annotation { "Feature Type Name" : "Feature", "Feature Type Description" : "" }
export const myFeature = defineFeature(function(context is Context, id is Id, definition is map)
    precondition{}
    {
        {
            var Q0;
            Q0=qCreatedBy(makeId("Right.planeOp"),FACE);
            var sketch = newSketch(context, id + "F0", { "sketchPlane" : qUnion([Q0])});
            skLineSegment(sketch, "E0", {"start": v(0, 0) * mm, "end": v(-381, 0) * mm});
            skLineSegment(sketch, "E1", {"start": v(0, 0) * mm, "end": v(381, 0) * mm});
            skLineSegment(sketch, "E2", {"start": v(0, 0) * mm, "end": v(0, 190.5) * mm});
            skLineSegment(sketch, "E3", {"start": v(-381, 0) * mm, "end": v(-457.2, 0) * mm});
            skLineSegment(sketch, "E4", {"start": v(-381, 0) * mm, "end": v(0, 190.5) * mm});
            skLineSegment(sketch, "E5", {"start": v(0, 190.5) * mm, "end": v(381, 0) * mm});
            skLineSegment(sketch, "E6", {"start": v(381, 0) * mm, "end": v(457.2, 0) * mm});
            skLineSegment(sketch, "E7", {"start": v(0, 190.5) * mm, "end": v(0, 228.6) * mm});
            skLineSegment(sketch, "E8", {"start": v(0, 228.6) * mm, "end": v(-457.2, 0) * mm});
            skLineSegment(sketch, "E9", {"start": v(0, 228.6) * mm, "end": v(457.2, 0) * mm});
            skLineSegment(sketch, "E10", {"start": v(-381, 0) * mm, "end": v(-381, -279.4) * mm});
            skLineSegment(sketch, "E11", {"start": v(381, 0) * mm, "end": v(381, -279.4) * mm});
            skLineSegment(sketch, "E12", {"start": v(381, -279.4) * mm, "end": v(-381, -279.4) * mm});
            skLineSegment(sketch, "E13", {"start": v(-381, -279.4) * mm, "end": v(-381, -330.2) * mm});
            skLineSegment(sketch, "E14", {"start": v(381, -279.4) * mm, "end": v(381, -330.2) * mm});
            skLineSegment(sketch, "E15", {"start": v(381, -330.2) * mm, "end": v(-381, -330.2) * mm});
            skLineSegment(sketch, "E16", {"start": v(381, -330.2) * mm, "end": v(762, -330.2) * mm});
            skLineSegment(sketch, "E17", {"start": v(762, -330.2) * mm, "end": v(762, -279.4) * mm});
            skLineSegment(sketch, "E18", {"start": v(762, -279.4) * mm, "end": v(381, -279.4) * mm});
            skLineSegment(sketch, "E19", {"start": v(762, -279.4) * mm, "end": v(762, -50.8) * mm});
            skLineSegment(sketch, "E20", {"start": v(762, -50.8) * mm, "end": v(381, 0) * mm});
            skLineSegment(sketch, "E21", {"start": v(762, -50.8) * mm, "end": v(762, -88.9) * mm});
            skLineSegment(sketch, "E22", {"start": v(762, -88.9) * mm, "end": v(381, -50.8) * mm});
            skLineSegment(sketch, "E23", {"start": v(-226.53, -279.4) * mm, "end": v(-226.53, -101.6) * mm});
            skLineSegment(sketch, "E24", {"start": v(-226.53, -101.6) * mm, "end": v(-150.33, -101.6) * mm});
            skLineSegment(sketch, "E25", {"start": v(-150.33, -101.6) * mm, "end": v(-150.33, -279.4) * mm});
            skLineSegment(sketch, "E26.0", {"start": v(-124.93, -76.2) * mm, "end": v(-124.93, -279.4) * mm});
            skLineSegment(sketch, "E26.1", {"start": v(-251.93, -76.2) * mm, "end": v(-124.93, -76.2) * mm});
            skLineSegment(sketch, "E26.2", {"start": v(-251.93, -279.4) * mm, "end": v(-251.93, -76.2) * mm});
            skLineSegment(sketch, "E27.bottom", {"start": v(50.8, -101.6) * mm, "end": v(279.4, -101.6) * mm});
            skLineSegment(sketch, "E27.top", {"start": v(50.8, -215.9) * mm, "end": v(279.4, -215.9) * mm});
            skLineSegment(sketch, "E27.left", {"start": v(50.8, -101.6) * mm, "end": v(50.8, -215.9) * mm});
            skLineSegment(sketch, "E27.right", {"start": v(279.4, -101.6) * mm, "end": v(279.4, -215.9) * mm});
            skLineSegment(sketch, "E28.0", {"start": v(38.1, -88.9) * mm, "end": v(38.1, -228.6) * mm});
            skLineSegment(sketch, "E28.1", {"start": v(38.1, -88.9) * mm, "end": v(292.1, -88.9) * mm});
            skLineSegment(sketch, "E28.2", {"start": v(292.1, -88.9) * mm, "end": v(292.1, -228.6) * mm});
            skLineSegment(sketch, "E28.3", {"start": v(38.1, -228.6) * mm, "end": v(292.1, -228.6) * mm});
            skLineSegment(sketch, "E29.bottom", {"start": v(508, -124.71) * mm, "end": v(609.6, -124.71) * mm});
            skLineSegment(sketch, "E29.top", {"start": v(508, -226.31) * mm, "end": v(609.6, -226.31) * mm});
            skLineSegment(sketch, "E29.left", {"start": v(508, -124.71) * mm, "end": v(508, -226.31) * mm});
            skLineSegment(sketch, "E29.right", {"start": v(609.6, -124.71) * mm, "end": v(609.6, -226.31) * mm});
            skLineSegment(sketch, "E30.0", {"start": v(520.7, -137.41) * mm, "end": v(596.9, -137.41) * mm});
            skLineSegment(sketch, "E30.1", {"start": v(520.7, -137.41) * mm, "end": v(520.7, -213.61) * mm});
            skLineSegment(sketch, "E30.2", {"start": v(520.7, -213.61) * mm, "end": v(596.9, -213.61) * mm});
            skLineSegment(sketch, "E30.3", {"start": v(596.9, -137.41) * mm, "end": v(596.9, -213.61) * mm});
            skText(sketch, "E31", { "text": "Sophia Davidson", "fontName": "OpenSans-Regular.ttf"});
            const initialGuessF0  = {"E31": [-0.83636, 0.2844, 1, 0, 0.09685]};
            skSetInitialGuess(sketch, initialGuessF0);
            skSolve(sketch);
        }
        {
            var Q0;
            Q0=makeQuery(id+"F0.imprint","IMPRINT",FACE,{"disambiguationData":[TD([[makeQuery(id+"F0.imprint","IMPRINT",EDGE,{"derivedFrom":sQuery(id+"F0.wireOp",EDGE,"E3")}),-1.0]])]});
            var Q1;
            Q1=makeQuery(id+"F0.imprint","IMPRINT",FACE,{"disambiguationData":[TD([[makeQuery(id+"F0.imprint","IMPRINT",EDGE,{"derivedFrom":sQuery(id+"F0.wireOp",EDGE,"E5")}),1.0]])]});
            extrude(context, id + "F1", {"entities" : qUnion([Q0, Q1]), "depth" : 454.15 * mm, "offsetDistance" : 30.48 * mm, "hasSecondDirection" : true, "secondDirectionOppositeDirection" : true, "secondDirectionDepth" : 496.82 * mm});
        }
        {
            var Q0;
            Q0=makeQuery(id+"F0.imprint","IMPRINT",FACE,{"disambiguationData":[TD([[makeQuery(id+"F0.imprint","IMPRINT",EDGE,{"derivedFrom":sQuery(id+"F0.wireOp",EDGE,"E1")}),1.0]])]});
            var Q1;
            Q1=makeQuery(id+"F0.imprint","IMPRINT",FACE,{"disambiguationData":[TD([[makeQuery(id+"F0.imprint","IMPRINT",EDGE,{"derivedFrom":sQuery(id+"F0.wireOp",EDGE,"E0")}),-1.0]])]});
            extrude(context, id + "F2", {"entities" : qUnion([Q0, Q1]), "operationType" : NewBodyOperationType.ADD, "endBound" : BoundingType.SYMMETRIC, "depth" : 755.9 * mm, "offsetDistance" : 30.48 * mm, "hasSecondDirection" : true, "secondDirectionOppositeDirection" : false, "secondDirectionDepth" : 307.85 * mm});
        }
        {
            var Q0;
            Q0=makeQuery(id+"F0.imprint","IMPRINT",FACE,{"disambiguationData":[TD([[makeQuery(id+"F0.imprint","IMPRINT",EDGE,{"derivedFrom":sQuery(id+"F0.wireOp",EDGE,"E0")}),1.0]])]});
            var Q1;
            {var subQ0=sQuery(id+"F0.wireOp",EDGE,"E20");Q1=makeQuery(id+"F0.imprint","IMPRINT",FACE,{"disambiguationData":[TD([[makeQuery(id+"F0.imprint","IMPRINT",EDGE,{"derivedFrom":subQ0}),1.0]])]});}
            var Q2;
            {var subQ0=sQuery(id+"F0.wireOp",EDGE,"E18");Q2=makeQuery(id+"F0.imprint","IMPRINT",FACE,{"disambiguationData":[TD([[makeQuery(id+"F0.imprint","IMPRINT",EDGE,{"derivedFrom":subQ0}),-1.0]])]});}
            extrude(context, id + "F3", {"entities" : qUnion([Q0, Q1, Q2]), "endBound" : BoundingType.SYMMETRIC, "depth" : 853.44 * mm, "offsetDistance" : 30.48 * mm});
        }
        {
            var Q0;
            {var subQ6=sQuery(id+"F0.wireOp",EDGE,"E13");Q0=makeQuery(id+"F0.imprint","IMPRINT",FACE,{"disambiguationData":[TD([[makeQuery(id+"F0.imprint","IMPRINT",EDGE,{"derivedFrom":subQ6}),1.0]])]});}
            var Q1;
            Q1=makeQuery(id+"F0.imprint","IMPRINT",FACE,{"disambiguationData":[TD([[makeQuery(id+"F0.imprint","IMPRINT",EDGE,{"derivedFrom":sQuery(id+"F0.wireOp",EDGE,"E14")}),1.0]])]});
            extrude(context, id + "F4", {"entities" : qUnion([Q0, Q1]), "operationType" : NewBodyOperationType.ADD, "endBound" : BoundingType.SYMMETRIC, "depth" : 859.54 * mm, "offsetDistance" : 30.48 * mm});
        }
        {
            var Q0;
            {var subQ0=sQuery(id+"F0.wireOp",EDGE,"E23");Q0=makeQuery(id+"F0.imprint","IMPRINT",FACE,{"disambiguationData":[TD([[makeQuery(id+"F0.imprint","IMPRINT",EDGE,{"derivedFrom":subQ0}),1.0]])]});}
            var Q1;
            Q1=makeQuery(id+"F0.imprint","IMPRINT",FACE,{"disambiguationData":[TD([[makeQuery(id+"F0.imprint","IMPRINT",EDGE,{"derivedFrom":sQuery(id+"F0.wireOp",EDGE,"E27.bottom")}),1.0]])]});
            var Q2;
            Q2=makeQuery(id+"F0.imprint","IMPRINT",FACE,{"disambiguationData":[TD([[makeQuery(id+"F0.imprint","IMPRINT",EDGE,{"derivedFrom":sQuery(id+"F0.wireOp",EDGE,"E29.bottom")}),-1.0]])]});
            extrude(context, id + "F5", {"entities" : qUnion([Q0, Q1, Q2]), "operationType" : NewBodyOperationType.ADD, "endBound" : BoundingType.SYMMETRIC, "depth" : 914.4 * mm, "offsetDistance" : 30.48 * mm});
        }
        {
            var Q0;
            Q0=makeQuery(id+"F0.imprint","IMPRINT",FACE,{"disambiguationData":[TD([[makeQuery(id+"F0.imprint","IMPRINT",EDGE,{"derivedFrom":sQuery(id+"F0.wireOp",EDGE,"E27.bottom")}),-1.0]])]});
            var Q1;
            {var subQ0=sQuery(id+"F0.wireOp",EDGE,"E23");Q1=makeQuery(id+"F0.imprint","IMPRINT",FACE,{"disambiguationData":[TD([[makeQuery(id+"F0.imprint","IMPRINT",EDGE,{"derivedFrom":subQ0}),-1.0]])]});}
            var Q2;
            Q2=makeQuery(id+"F0.imprint","IMPRINT",FACE,{"disambiguationData":[TD([[makeQuery(id+"F0.imprint","IMPRINT",EDGE,{"derivedFrom":sQuery(id+"F0.wireOp",EDGE,"E30.0")}),-1.0]])]});
            extrude(context, id + "F6", {"entities" : qUnion([Q0, Q1, Q2]), "operationType" : NewBodyOperationType.ADD, "endBound" : BoundingType.SYMMETRIC, "depth" : 30.48 * mm, "offsetDistance" : 30.48 * mm});
        }
    });